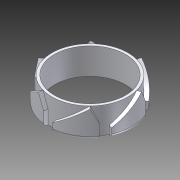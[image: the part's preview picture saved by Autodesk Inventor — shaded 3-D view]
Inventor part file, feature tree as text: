
AUTODESK INVENTOR PART (.ipt)
format: ipt  version: 2012 (Build 160160000, 160)  size: 229,376 bytes
history: native  units: mm
features: sketch x4, extrude x2, pattern_circular x2, helix x2, fillet x1
ambient origin geometry x8: Origin, YZ Plane, XZ Plane, XY Plane, X Axis, Y Axis, Z Axis, Center Point
bodies: Solid1 (feature_tree)
feature tree (11):
  sketch  "Sketch1"  dims[d0=64.0mm d1=54.0mm d2=50.0mm]
  extrude  "Extrusion2"  Depth=54.0mm
  sketch  "Sketch3"  dims[d3=58.0mm d6=20.0mm d7=0.0mm]
  fillet  "Fillet3"  Radius=50.0mm
  sketch  "Sketch5"  dims[d10=4.0mm]
  extrude  "Extrusion9"  Depth=20.0mm TaperAngle=0.0deg
  pattern_circular  "Circular Pattern6"  [2 undecoded]
  sketch  "Sketch7"  dims[d17=2.0mm d35=44.1mm d36=55.0mm d37=1.012291mm d46=2.0mm d47=4.0mm d58=4.0mm d59=26.0mm d86=2.094395mm d87=10.0mm d88=0.0mm d89=60.0mm d90=360.0deg d92=1.047198mm d93=29.0mm d94=22.0mm d95=10.0mm d96=16.0mm d97=1.25mm d98=0.0mm d99=90.0deg d100=90.0deg d101=0.0mm d102=0.0mm d103=16.0mm d104=10.0mm d105=16.0mm d106=0.416667mm d107=0.0mm d108=90.0deg d109=90.0deg d110=0.0mm d111=0.0mm d112=60.0mm d113=360.0deg d115=18.0mm]
  helix  "Coil5"  [1 undecoded]
  helix  "Coil6"  [1 undecoded]
  pattern_circular  "Circular Pattern7"  [2 undecoded]
note: 6 required parameter values undecoded (feature->parameter linkage not recoverable at this tier; creation-order binding heuristic only, values carry confidence <= 0.55)
